# Revit family: HOSPIVAC G SIRELLA
name_source: partatom
category: Equipement de génie climatique
revit_build: Autodesk Revit 2018 (Build: 20170223_1515(x64)
units: mm (PartAtom-declared; Revit-internal decimal feet)

## family parameters
Basée sur le plan de construction = Non
Classification = Aucun
Cote de connecteur circulaire = Utiliser le diamètre
Couper avec des vides une fois chargée = Non
Partagée = Non
Point de calcul de pièce = Non
Toujours verticalement = Oui
Type d'élément = Normal

## types (3) — shared parameters
COS_PHI = 0.9
DESCR_ALIM = Alimentation ; 4G2.5mm²
DOUBLE_ALIMENTATION = Non
ENTRAXE_LARG_FIX_SOL = 500 mm  [stored 1.64042 ft]
EP_AILE = 8.5 mm  [stored 0.0278871 ft]
EP_AME = 6 mm  [stored 0.019685 ft]
Fabricant = MIL'S
LARGEUR = 550 mm  [stored 1.80446 ft]
LARG_PROFIL = 50 mm  [stored 0.164042 ft]
LONG_PROFILE = 550 mm  [stored 1.80446 ft]
Lien espace client = https://www.mils.fr
Modèle = HOSPIVAC G SIRELLA
NBR_POLES = 3
NEUTRE = Non
OFFSET_HAUT_PROFILE = 100 mm  [stored 0.328084 ft]
OFFSET_LONG_PPE = 37 mm  [stored 0.121391 ft]
TENSION_ALIM = 400 V
TERRE = Oui
ZONE_DE_MAINTENANCE = Oui
ØPERCAGE = 13 mm

## per-type parameters (varying)
- HOSPIVAC G SL300.R: DEBIT_ASPI_VIDE=260.0 m³/h; DEBIT_REFOUL_VIDE=260.0 m³/h; DEGAG_CALORIFIQUE(kJ/h)=22738; DESCR_ASPI=Aspiration ; 260 m³/h ; Flexible avec clapet G 2"; DESCR_REFOUL=Refoulement ; 260 m³/h ; Flexible avec raccord G 2" mâle; DIAM_ASPI_VIDE=50 mm  [stored 0.164042 ft]; DIAM_REFOUL_VIDE=50 mm  [stored 0.164042 ft]; ENTRAXE_LONG_FIX_SOL=680 mm  [stored 2.23097 ft]; ENTRAXE_PROFILE=730 mm  [stored 2.39501 ft]; FREQUENCE=0 Hz; HAUTEUR=780 mm  [stored 2.55906 ft]; HAUT_REFOUL=164 mm  [stored 0.538058 ft]; LARG_MAINT=872.4 mm; LONGUEUR=910 mm; LONG_COUDE=58 mm  [stored 0.190289 ft]; LONG_REFOUL=105.4 mm; NIVEAU_SONORE(dB(A))=70; OFFSET_HAUT_BRIDE=668.1 mm  [stored 2.19193 ft]; OFFSET_HAUT_COUD=743 mm  [stored 2.43766 ft]; OFFSET_HAUT_MAINT=914.2 mm; OFFSET_HAUT_PPE=24.4 mm  [stored 0.0800525 ft]; OFFSET_LARG_REFOUL=93.4 mm  [stored 0.30643 ft]; OFFSET_LONG_COUD=270.3 mm; OFFSET_LONG_MAINT_1=600.4 mm; OFFSET_LONG_MAINT_2=689.8 mm; POIDS(Kg)=310 mm  [stored 1.01706 ft]; PROTEC_ELECT=Disjoncteur courbe D - 16 A; PUISS_APPARENTE=6111 VA; PUISS_ELECT=6 kW; TYPE_PPE=SIRELLA SLR : SL300.R; ØCANA=50 mm  [stored 0.164042 ft]
- HOSPIVAC G SL150.R: DEBIT_ASPI_VIDE=140.0 m³/h; DEBIT_REFOUL_VIDE=140.0 m³/h; DEGAG_CALORIFIQUE(kJ/h)=12403; DESCR_ASPI=Aspiration ; 140 m³/h ; Flexible avec clapet G 1"1/2; DESCR_REFOUL=Refoulement ; 140 m³/h ; Flexible avec raccord G 1"1/2 mâle; DIAM_ASPI_VIDE=40 mm  [stored 0.131234 ft]; DIAM_REFOUL_VIDE=40 mm  [stored 0.131234 ft]; ENTRAXE_LONG_FIX_SOL=605 mm  [stored 1.98491 ft]; ENTRAXE_PROFILE=655 mm  [stored 2.14895 ft]; FREQUENCE=0 Hz; HAUTEUR=700 mm  [stored 2.29659 ft]; HAUT_REFOUL=149 mm; LARG_MAINT=825 mm; LONGUEUR=800 mm  [stored 2.62467 ft]; LONG_COUDE=50 mm  [stored 0.164042 ft]; LONG_REFOUL=72 mm  [stored 0.23622 ft]; NIVEAU_SONORE(dB(A))=69; OFFSET_HAUT_BRIDE=605 mm  [stored 1.98491 ft]; OFFSET_HAUT_COUD=670 mm  [stored 2.19816 ft]; OFFSET_HAUT_MAINT=905 mm; OFFSET_HAUT_PPE=15.2 mm; OFFSET_LARG_REFOUL=120 mm  [stored 0.393701 ft]; OFFSET_LONG_COUD=232 mm  [stored 0.761155 ft]; OFFSET_LONG_MAINT_1=570 mm  [stored 1.87008 ft]; OFFSET_LONG_MAINT_2=610 mm  [stored 2.00131 ft]; POIDS(Kg)=185 mm  [stored 0.606955 ft]; PROTEC_ELECT=Disjoncteur courbe D - 10 A; PUISS_APPARENTE=3333 VA; PUISS_ELECT=3 kW; TYPE_PPE=SIRELLA SLR : SL150.R; ØCANA=45 mm  [stored 0.147638 ft]
- HOSPIVAC G SL100.R: DEBIT_ASPI_VIDE=90.0 m³/h; DEBIT_REFOUL_VIDE=90.0 m³/h; DEGAG_CALORIFIQUE(kJ/h)=9095; DESCR_ASPI=Aspiration ; 90 m³/h ; Flexible avec clapet G 1"1/2; DESCR_REFOUL=Refoulement ; 90 m³/h ; Flexible avec raccord G 1"1/2 mâle; DIAM_ASPI_VIDE=40 mm  [stored 0.131234 ft]; DIAM_REFOUL_VIDE=40 mm  [stored 0.131234 ft]; ENTRAXE_LONG_FIX_SOL=605 mm  [stored 1.98491 ft]; ENTRAXE_PROFILE=655 mm  [stored 2.14895 ft]; FREQUENCE=50 Hz; HAUTEUR=700 mm  [stored 2.29659 ft]; HAUT_REFOUL=149 mm; LARG_MAINT=825 mm; LONGUEUR=800 mm  [stored 2.62467 ft]; LONG_COUDE=50 mm  [stored 0.164042 ft]; LONG_REFOUL=72 mm  [stored 0.23622 ft]; NIVEAU_SONORE(dB(A))=69; OFFSET_HAUT_BRIDE=604.6 mm  [stored 1.9836 ft]; OFFSET_HAUT_COUD=670 mm  [stored 2.19816 ft]; OFFSET_HAUT_MAINT=905 mm; OFFSET_HAUT_PPE=15.2 mm; OFFSET_LARG_REFOUL=120 mm  [stored 0.393701 ft]; OFFSET_LONG_COUD=231.5 mm  [stored 0.759514 ft]; OFFSET_LONG_MAINT_1=570 mm  [stored 1.87008 ft]; OFFSET_LONG_MAINT_2=610 mm  [stored 2.00131 ft]; POIDS(Kg)=175 mm  [stored 0.574147 ft]; PROTEC_ELECT=Disjoncteur courbe D - 10 A; PUISS_APPARENTE=2444 VA; PUISS_ELECT=2 kW; TYPE_PPE=SIRELLA SLR : SL100.R; ØCANA=45 mm  [stored 0.147638 ft]

note: [stored X ft] marks values corroborated as IEEE doubles in the binary element streams (Revit-internal decimal feet)
